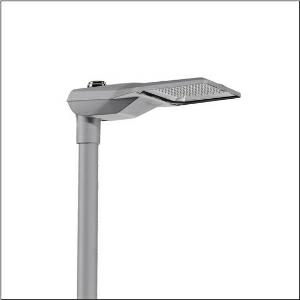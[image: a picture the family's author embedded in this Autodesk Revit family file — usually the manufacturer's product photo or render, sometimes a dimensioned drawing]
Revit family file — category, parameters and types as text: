
# Revit family: streetlight_sl_21_midi___st0_8a_5xe7c37n08mb_215a
name_source: partatom
category: Lighting Fixtures
units: mm (PartAtom-declared; Revit-internal decimal feet)

## family parameters
Cut with Voids When Loaded = No
Host = Face
Light Source = No
Part Type = Normal
Room Calculation Point = No
Round Connector Dimension = Use Diameter
Shared = No

## types (1)
- --- (1 x LED, 18270 lm, 136 W, 3000K)
    Apparent Load = 136 VA
    CIE Flux Codes = 38 75 97 100 100
    Color Rendering = 70
    Color Temperature = 3000K
    Default Elevation = 1800 mm
    Description = Streetlight SL 21 midi, mast luminaire, primary light control with lens, of PMMA, primary optical cover: cover, of toughened safety glass, transparent, light distribution: ST0.8a, light emission: direct distribution, primary light characteristic: asymmetric, installation type: side-entry, LED, 3G 2.5mm², High Power LED, rated luminous flux: 18.270lm, luminous efficacy: 134lm/W, light colour: 730, colour temperature: 3000K, control gear: NEMA (7pin), control: overheat protection, pre-setting: linear dimming characteristic, constant luminous flux control, time-dependent luminous flux control, flexible luminous flux parameterisation, mains connection: 220..240V, AC, 50/60Hz, connection cable pre-assembled, cable length: 12,5m, wiring characteristics: H05VV-F, start of lifetime: 136W, end of service life: 142W, reduction: 61W, luminaire housing, of diecast aluminium (EN AC-44300), powder-coated, Siteco® metallic grey (DB 702S), corrosivity category C5 mid according to DIN EN ISO 12944, multi-level sealing system, sealing non-destructively replaceable, inclination adjustable: 0°, 5°, 10°, 15°, length: 644mm, width: 335mm, height: 110mm, spigot size: 42mm (side-entry), mounting height: 4..8m, protection rating (complete): IP66, insulation class (complete): insulation class I (protective earthing), certification: CE, ENEC, ENEC+, VDE, impact resistance: IK10, permissible operating ambient temperature for outdoor applications: -40..+50°C, standard-compliant lighting for roads and squares, packaging unit: 1 piece

Light Distribution: ST0.8a
    Height = 111 mm
    Lamp = 1 x LED
    Lamp Light Flux = 18270 lm
    Lamp Power = 136 W
    Lamp count = 1
    Length = 644 mm
    Luminous efficacy = 134 lm/W
    Manufacturer = Siteco
    ModVariant = No
    Model = 5XE7C37N08MB
    Number of Poles = 1
    OnlyDefault = Yes
    Power Factor = 1
    Product Name = Streetlight SL 21 midi | ST0.8a
    Product group = mast luminaire | pylon top
    ProductGroupID = 6100
    Protection Class = Protection class I
    Protection Degree = IP 66
    RLX_Detail_Level = 1
    RLX_Emergency_Light_Flux = 0 lm
    RLX_Emergency_Type = 0
    RLX_Emergency_Type_DB = No
    RlxData = <blob elided: 26557 chars, md5=4924356c>
    Socket = socket
    Standby Power = 0 W
    System Light Flux = 18270 lm
    System Power = 136 W
    Type Comments = factory setting: luminous flux: 100 % | dim-lin: 254 | 695 mA
    Type Image = l_1294377.jpg
    URL = http://relux.com
    VarID = @adj_155549
    Voltage = 0 V
    Weight = 0.00 kg
    Width = 336 mm

## geometry (parser evidence)
native form markers: Blend x4, Sweep x10
no freeform markers — native parametric forms only
